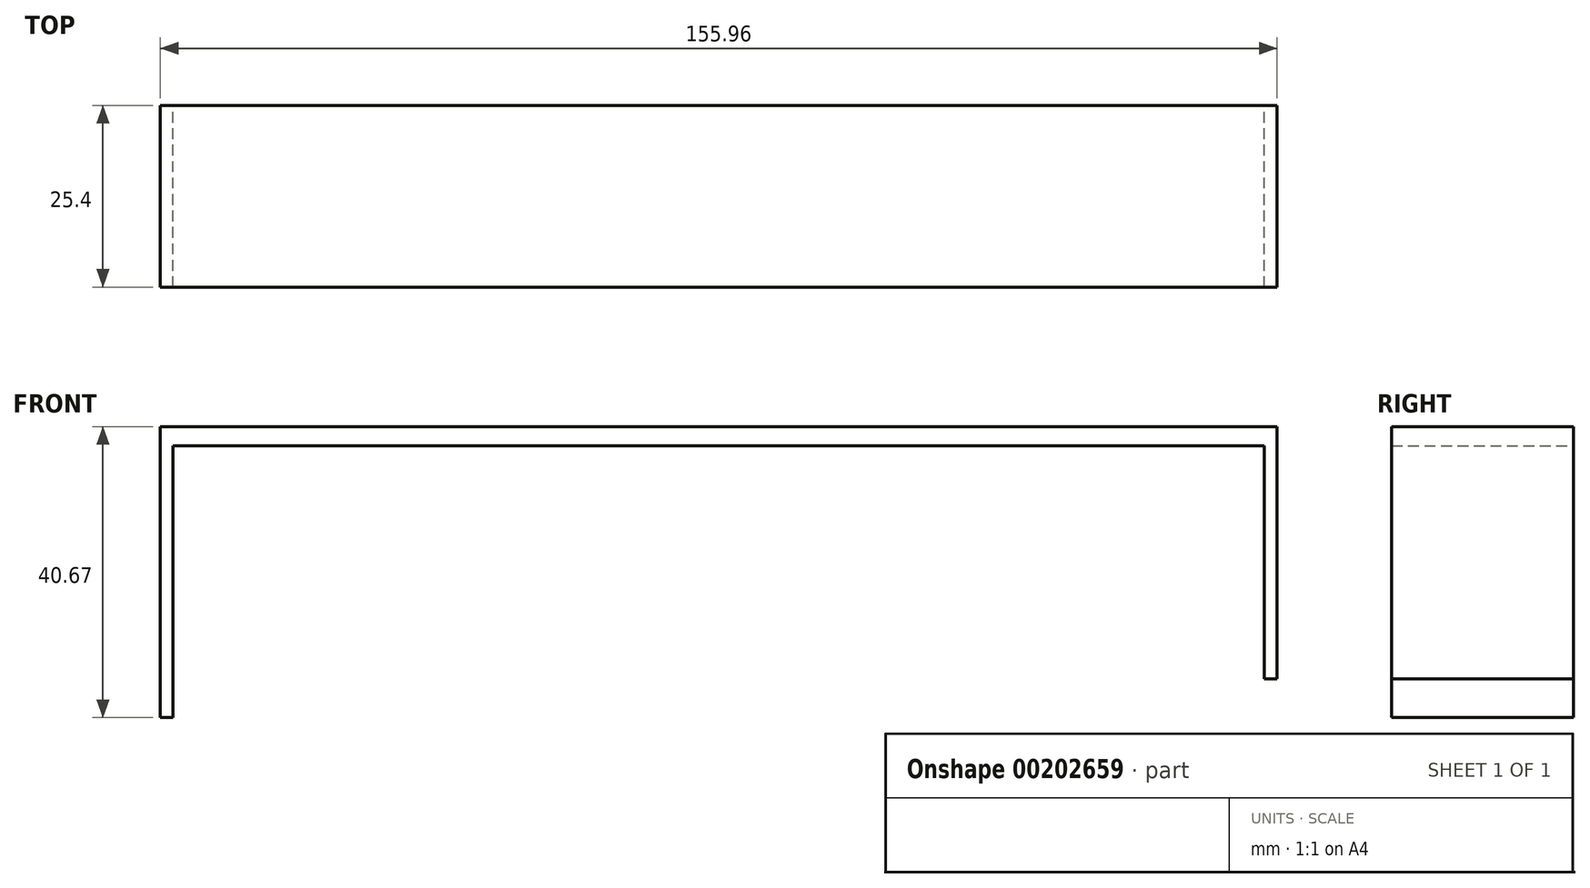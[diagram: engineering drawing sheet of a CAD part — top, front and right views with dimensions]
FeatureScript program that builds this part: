
annotation { "Feature Type Name" : "Feature", "Feature Type Description" : "" }
export const myFeature = defineFeature(function(context is Context, id is Id, definition is map)
    precondition{}
    {
        {
            var Q0;
            Q0=qCreatedBy(makeId("Front.planeOp"),FACE);
            var sketch = newSketch(context, id + "F0", { "sketchPlane" : qUnion([Q0])});
            skLineSegment(sketch, "E0", {"start": v(-95.74, -3.41) * mm, "end": v(-95.74, 37.21) * mm});
            skLineSegment(sketch, "E1", {"start": v(-95.74, 37.21) * mm, "end": v(60.22, 37.21) * mm});
            skLineSegment(sketch, "E2", {"start": v(60.22, 1.94) * mm, "end": v(60.22, 37.21) * mm});
            skLineSegment(sketch, "E3", {"start": v(58.44, 1.94) * mm, "end": v(60.22, 1.94) * mm});
            skLineSegment(sketch, "E4", {"start": v(58.44, 1.94) * mm, "end": v(58.44, 34.56) * mm});
            skLineSegment(sketch, "E5", {"start": v(58.44, 34.56) * mm, "end": v(-93.96, 34.56) * mm});
            skLineSegment(sketch, "E6", {"start": v(-93.96, 34.56) * mm, "end": v(-93.96, -3.46) * mm});
            skLineSegment(sketch, "E7", {"start": v(-93.96, -3.46) * mm, "end": v(-95.74, -3.41) * mm});
            skSolve(sketch);
        }
        {
            var Q0;
            Q0 = qSketchRegion(id + "F0", true);
            extrude(context, id + "F1", {"entities" : qUnion([Q0]), "depth" : 25.4 * mm});
        }
    });
